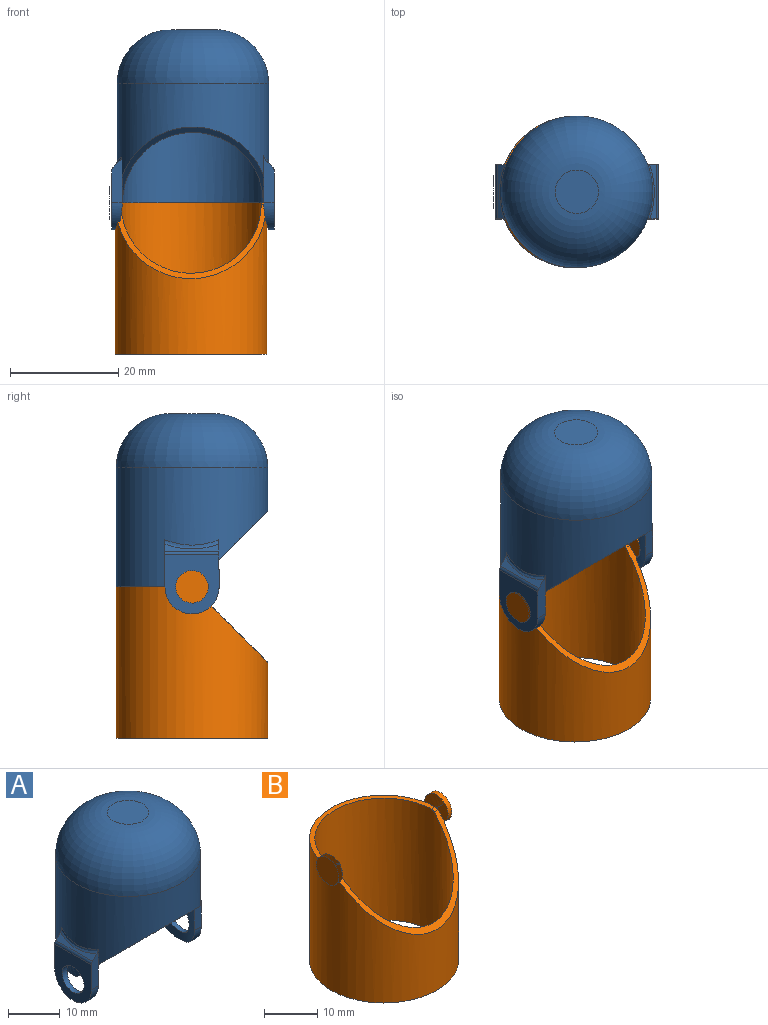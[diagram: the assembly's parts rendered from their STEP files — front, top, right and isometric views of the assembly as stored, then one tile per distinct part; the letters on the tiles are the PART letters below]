
ASSEMBLY  parts=2 mates=1
PART A: 30 faces, bbox 30x28x37 mm
  f0: cylinder r=14mm len=5.12mm, axis (0,0,-1), area 10.6mm2, adj f3,f9,f20,f23
  f1: cylinder r=14mm len=28mm, axis (0,0,-1), area 1391mm2, adj f3,f6,f9,f11,f15,f17,f21,f26
  f2: cylinder r=14mm len=5.12mm, axis (0,0,-1), area 10.6mm2, adj f3,f9,f13,f22
  f3: plane 27.99x13.59mm, normal (0,0,-1), area 41.6mm2, adj f0,f1,f2,f4,f10,f16,f22,f23
  f4: cylinder r=13mm len=26mm, axis (0,0,-1), area 1458.9mm2, adj f3,f8,f9,f22,f23
  f5: plane 8x8mm, normal (0,0,1), area 50.3mm2, adj f6
  f6: torus R=4mm, axis (0,0,1), area 1023.1mm2, adj f1,f5
  f7: plane 8x8mm, normal (0,0,-1), area 50.3mm2, adj f8
  f8: torus R=4mm, axis (0,0,1), area 864.2mm2, adj f4,f7
  f9: plane 28x13.71mm, normal (0,-0.71,-0.71), area 59.2mm2, adj f0,f1,f2,f4,f10,f16,f22,f23
  f10: cylinder r=14mm len=10mm, axis (0,0,-1), area 35mm2, adj f3,f9,f11,f13,f14,f15
  f11: plane 8.76x1.96mm, normal (0,1,0), area 14.1mm2, adj f1,f10,f12,f14,f24,f27,f29
  f12: plane 10.89x10.02mm, normal (1,0,0), area 69.9mm2, adj f11,f13,f14,f15,f29
  f13: cylinder r=3mm len=6mm, axis (1,0,0), area 21.9mm2, adj f2,f10,f12
  f14: cylinder r=5mm len=10mm, axis (1,0,0), area 30.2mm2, adj f10,f11,f12,f15
  f15: plane 8.7x1.95mm, normal (0,-1,0), area 13.9mm2, adj f1,f10,f12,f14,f24,f27,f29
  f16: cylinder r=14mm len=10mm, axis (0,0,-1), area 35mm2, adj f3,f9,f17,f18,f20,f21
  f17: plane 8.76x1.96mm, normal (0,1,0), area 14.1mm2, adj f1,f16,f18,f19,f25,f26,f28
  f18: cylinder r=5mm len=10mm, axis (-1,0,0), area 30.2mm2, adj f16,f17,f19,f21
  f19: plane 10.89x10.02mm, normal (-1,0,0), area 69.9mm2, adj f17,f18,f20,f21,f28
  f20: cylinder r=3mm len=6mm, axis (-1,0,0), area 23.4mm2, adj f0,f16,f19
  f21: plane 8.7x1.95mm, normal (0,-1,0), area 13.9mm2, adj f1,f16,f18,f19,f25,f26,f28
  f22: cylinder r=1mm len=1mm, axis (-1,0,0), area 0.8mm2, adj f2,f3,f4,f9
  f23: cylinder r=1mm len=1mm, axis (-1,0,0), area 0.8mm2, adj f0,f3,f4,f9
  f24: plane 10.01x1.28mm, normal (0.71,0,0.71), area 9.9mm2, adj f11,f15,f27,f29
  f25: plane 10.01x1.28mm, normal (-0.71,0,0.71), area 9.9mm2, adj f17,f21,f26,f28
  f26: bspline ~10.71x1.71mm, area 8.4mm2, adj f1,f17,f21,f25
  f27: bspline ~10.71x1.71mm, area 8.4mm2, adj f1,f11,f15,f24
  f28: cylinder r=1mm len=10mm, axis (0,-1,0), area 7.9mm2, adj f17,f19,f21,f25
  f29: cylinder r=1mm len=10mm, axis (0,-1,0), area 7.9mm2, adj f11,f12,f15,f24
PART B: 18 faces, bbox 42x40x43 mm
  f0: plane 27.99x13.59mm, normal (0,0,1), area 41.6mm2, adj f1,f2,f3,f4,f5,f6
  f1: cylinder r=13mm len=28mm, axis (0,0,-1), area 1949mm2, adj f0,f2,f6,f7,f8
  f2: cylinder r=1mm len=1.01mm, axis (-1,0,0), area 0.8mm2, adj f0,f1,f3,f7,f9
  f3: cylinder r=14mm len=5.12mm, axis (0,0,-1), area 10.7mm2, adj f0,f2,f9,f10,f11
  f4: cylinder r=14mm len=28mm, axis (0,0,-1), area 2049.7mm2, adj f0,f7,f8,f10,f12
  f5: cylinder r=14mm len=5.12mm, axis (0,0,-1), area 10.7mm2, adj f0,f6,f12,f13,f14
  f6: cylinder r=1mm len=1.01mm, axis (-1,0,0), area 0.8mm2, adj f0,f1,f5,f7,f13
  f7: plane 28x13.71mm, normal (0,-0.71,0.71), area 59.5mm2, adj f1,f2,f4,f6,f9,f10,f12,f13
  f8: plane 28x28mm, normal (0,0,-1), area 84.8mm2, adj f1,f4
  f9: plane 4.24x3mm, normal (-1,0,0), area 7.1mm2, adj f2,f3,f7,f10,f11
  f10: cylinder r=3mm len=6mm, axis (1,0,0), area 20.7mm2, adj f3,f4,f7,f9,f11,f15
  f11: plane 2.13x2.13mm, normal (0,-0.71,-0.71), area 0.2mm2, adj f3,f9,f10
  f12: cylinder r=3mm len=6mm, axis (-1,0,0), area 4.3mm2, adj f4,f5,f7,f13,f14
  f13: plane 4.24x3mm, normal (1,0,0), area 7.1mm2, adj f5,f6,f7,f12,f14
  f14: plane 2.13x2.13mm, normal (0,-0.71,-0.71), area 0.2mm2, adj f5,f12,f13
  f15: plane 6x6mm, normal (1,0,0), area 28.3mm2, adj f10
  f16: plane 18x18mm, normal (1,0,0), area 28.3mm2, adj f17
  f17: cylinder r=3mm len=2.12mm, axis (-1,0,0), area 0mm2, adj f16
PLACE A rot(axis=(1,0,0),0deg) t=(-66.67,-40.75,-3.38)mm
PLACE B rot(axis=(1,0,0),0deg) t=(-67.01,-40.75,-3.38)mm fixed
MATE revolute B.f10 <-> A.f13  axis (-1,0,0) through (-53.01,-40.75,24.62)mm
